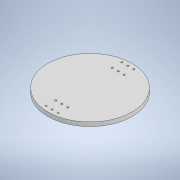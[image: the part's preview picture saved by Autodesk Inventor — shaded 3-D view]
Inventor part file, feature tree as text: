
AUTODESK INVENTOR PART (.ipt)
format: ipt  version: 2021 (Build 250183000, 183)  size: 161,280 bytes
history: native  units: mm
features: extrude x4, sketch x4
ambient origin geometry x8: Origin, YZ Plane, XZ Plane, XY Plane, X Axis, Y Axis, Z Axis, Center Point
bodies: Solid1 (feature_tree)
feature tree (8):
  extrude  "Extrusion1"  Depth=10.0mm TaperAngle=0.0deg
  extrude  "Extrusion2"  Depth=10.0mm TaperAngle=0.0deg
  extrude  "Extrusion3"  Depth=15.0mm
  extrude  "Extrusion4"  Depth=10.0mm
  sketch  "Sketch1"  dims[d0=210.0mm d1=10.0mm d2=0.0mm]
  sketch  "Sketch2"  dims[d3=5.0mm d4=10.0mm d5=0.0mm]
  sketch  "Sketch3"  dims[d9=75.0mm d10=15.0mm]
  sketch  "Sketch4"  dims[d19=5.0mm d20=5.0mm d21=5.0mm d25=5.0mm d26=5.0mm d27=5.0mm d28=5.0mm d29=5.0mm d30=5.0mm d31=5.0mm d32=5.0mm d33=5.0mm d34=5.0mm d35=5.0mm d36=5.0mm d37=10.0mm d38=0.0mm d39=4.0mm d40=4.0mm d41=4.0mm d42=4.0mm d43=4.0mm d44=4.0mm d45=4.0mm d46=4.0mm d47=4.0mm d48=4.0mm d49=4.0mm d50=4.0mm d51=10.0mm d52=0.0mm]
